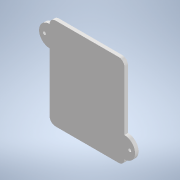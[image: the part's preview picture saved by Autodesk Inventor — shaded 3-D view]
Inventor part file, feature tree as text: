
AUTODESK INVENTOR PART (.ipt)
format: ipt  version: 2021 (Build 250183000, 183)  size: 141,824 bytes
history: native  units: mm
features: reference x11, other x3, extrude x2, sketch x2
ambient origin geometry x8: Origin, YZ Plane, XZ Plane, XY Plane, X Axis, Y Axis, Z Axis, Center Point
bodies: Body1 (feature_tree)
feature tree (18):
  extrude  "Extrusion3"  Depth=3.0mm
  extrude  "Extrusion4"  Depth=2.0mm TaperAngle=0.0deg
  sketch  "Sketch3"  dims[d6=3.0mm d7=0.0mm d8=0.2mm]
  reference  "Reference6"
  reference  "Reference7"
  reference  "Reference8"
  reference  "Reference9"
  sketch  "Sketch5"  dims[d9=1.0mm d10=2.0mm d11=0.0mm]
  reference  "Reference12"
  reference  "Reference13"
  reference  "Reference14"
  reference  "Reference15"
  reference  "Reference16"
  reference  "Reference17"
  reference  "Reference18"
  other  "<userpath>\Desktop\Motion_capture\MAIN\Models_3D\Arm_box\armbox_assembly.iam"
  other  "armbox_assembly.iam"
  other  "arm_box:1"
